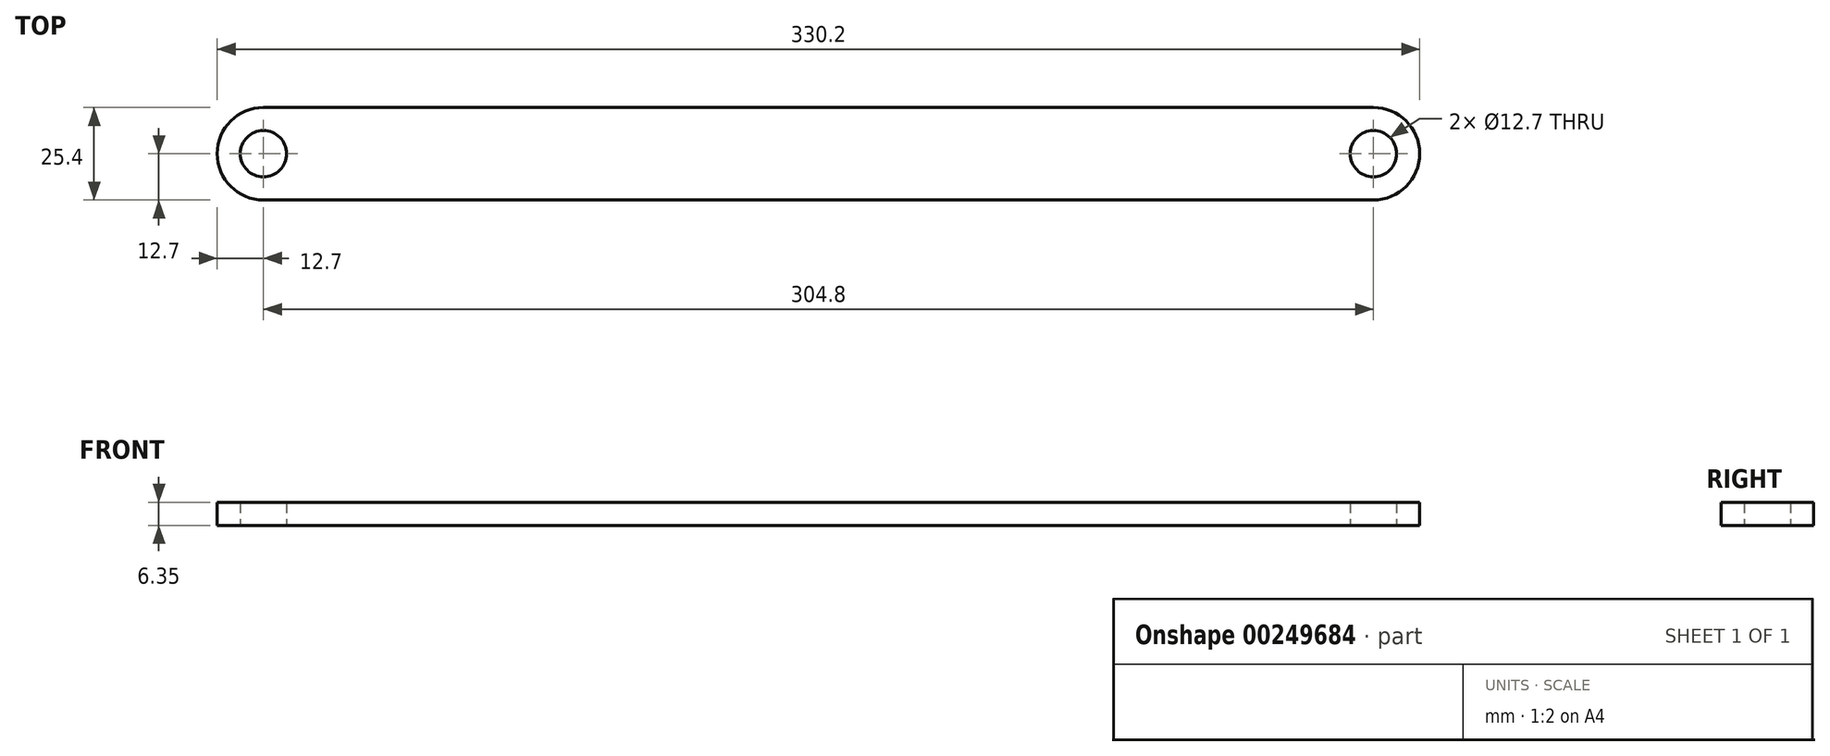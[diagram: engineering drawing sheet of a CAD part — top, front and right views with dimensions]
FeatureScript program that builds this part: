
annotation { "Feature Type Name" : "Feature", "Feature Type Description" : "" }
export const myFeature = defineFeature(function(context is Context, id is Id, definition is map)
    precondition{}
    {
        {
            var Q0;
            Q0=qCreatedBy(makeId("Top.planeOp"),FACE);
            var sketch = newSketch(context, id + "F0", { "sketchPlane" : qUnion([Q0])});
            skArc(sketch, "E0", {"start": v(-317.5, 12.7) * mm, "mid": v(-330.2, 0) * mm, "end": v(-317.5, -12.7) * mm});
            skArc(sketch, "E1", {"start": v(-12.7, -12.7) * mm, "mid": v(0, 0) * mm, "end": v(-12.7, 12.7) * mm});
            skLineSegment(sketch, "E2", {"start": v(-317.5, 12.7) * mm, "end": v(-12.7, 12.7) * mm});
            skLineSegment(sketch, "E3", {"start": v(-317.5, -12.7) * mm, "end": v(-12.7, -12.7) * mm});
            skCircle(sketch, "E4", {"center": v(-12.7, 0) * mm, "radius": 6.35 * mm});
            skCircle(sketch, "E5", {"center": v(-317.5, 0) * mm, "radius": 6.35 * mm});
            skSolve(sketch);
        }
        {
            var Q0;
            Q0=makeQuery(id+"F0.imprint","IMPRINT",FACE,{"disambiguationData":[TD([[makeQuery(id+"F0.imprint","IMPRINT",EDGE,{"derivedFrom":sQuery(id+"F0.wireOp",EDGE,"E0")}),1.0]])]});
            extrude(context, id + "F1", {"entities" : qUnion([Q0]), "depth" : 6.35 * mm});
        }
    });
